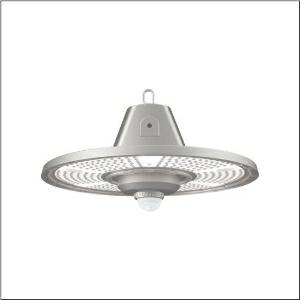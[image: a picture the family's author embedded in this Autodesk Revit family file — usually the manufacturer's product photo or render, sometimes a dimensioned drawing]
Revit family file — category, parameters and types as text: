
# Revit family: highbay_31-l_51hc427a4mmb01
name_source: partatom
category: Lighting Fixtures
units: mm (PartAtom-declared; Revit-internal decimal feet)

## family parameters
Cut with Voids When Loaded = No
Host = Face
Light Source = No
Part Type = Normal
Room Calculation Point = No
Round Connector Dimension = Use Diameter
Shared = No

## types (1)
- Highbay 31-L (1 x LED, 28000 lm, 187 W, 4000K)
    Apparent Load = 187 VA
    CIE Flux Codes = 83 98 100 100 100
    Color Rendering = 80
    Color Temperature = 4000K
    Default Elevation = 1800 mm
    Description = Highbay 31-L, high bay luminaire, primary light control with lens, of PC, primary optical cover: cover panel, of PC, transparent, light emission: direct distribution, primary light characteristic: rotationally symmetric, installation type: suspended mounting, surface-mounted, LED, rated luminous flux: 28.000lm, luminous efficacy: 150lm/W, light colour: 840, colour temperature: 4000K, control gear: ON/OFF, with cable, 3x 1.0mm², free wire ends, mains connection: 220..240V, AC/DC, 0/50..60Hz, cable length: 1,5m, rated input power: 187W, housing, rotationally symmetric, of diecast aluminium, powder-coated, grey aluminium (RAL 9007), with hook on luminaire side, incl. screw, diameter: 406mm, PIR sensor, protection rating (complete): IP65, insulation class (complete): insulation class I (protective earthing), certification: CE, ENEC, UKCA, protection symbol: D, impact resistance: IK08, permissible operating ambient temperature: -30..+45°C, standard: EN 60598-2-22, EN 60598, corresponds to IFS (International Featured Standards) requirements for safety and quality in the food industry, packaging unit: 1 piece
    Height = 160 mm
    Lamp = 1 x LED
    Lamp Light Flux = 28000 lm
    Lamp Power = 187 W
    Lamp count = 1
    Length = 406 mm
    Luminous efficacy = 150 lm/W
    Manufacturer = Siteco
    ModVariant = No
    Model = 51HC427A4MMB01
    Mounting Place = Ceiling
    Mounting Type = Pendant
    Number of Poles = 1
    OnlyDefault = Yes
    Power Factor = 1
    Product Name = Highbay 31-L
    Product group = high bay luminaire
    ProductGroupID = 901
    Protection Class = Protection class I
    Protection Degree = IP 65
    RLX_Detail_Level = 1
    RLX_Emergency_Light_Flux = 0 lm
    RLX_Emergency_Type = 0
    RLX_Emergency_Type_DB = No
    RlxData = <blob elided: 122317 chars, md5=40b38b48>
    Socket = socket
    Standby Power = 0 W
    System Light Flux = 28000 lm
    System Power = 187 W
    Type Comments = Product without accessories
    Type Image = l_384981.jpg
    URL = http://relux.com
    VarID = ---
    Voltage = 0 V
    Weight = 0.00 kg
    Width = 0 mm  [stored 0 ft]

note: [stored X ft] marks values corroborated as IEEE doubles in the binary element streams (Revit-internal decimal feet)

## geometry (parser evidence)
native form markers: Blend x4, Sweep x10
no freeform markers — native parametric forms only
